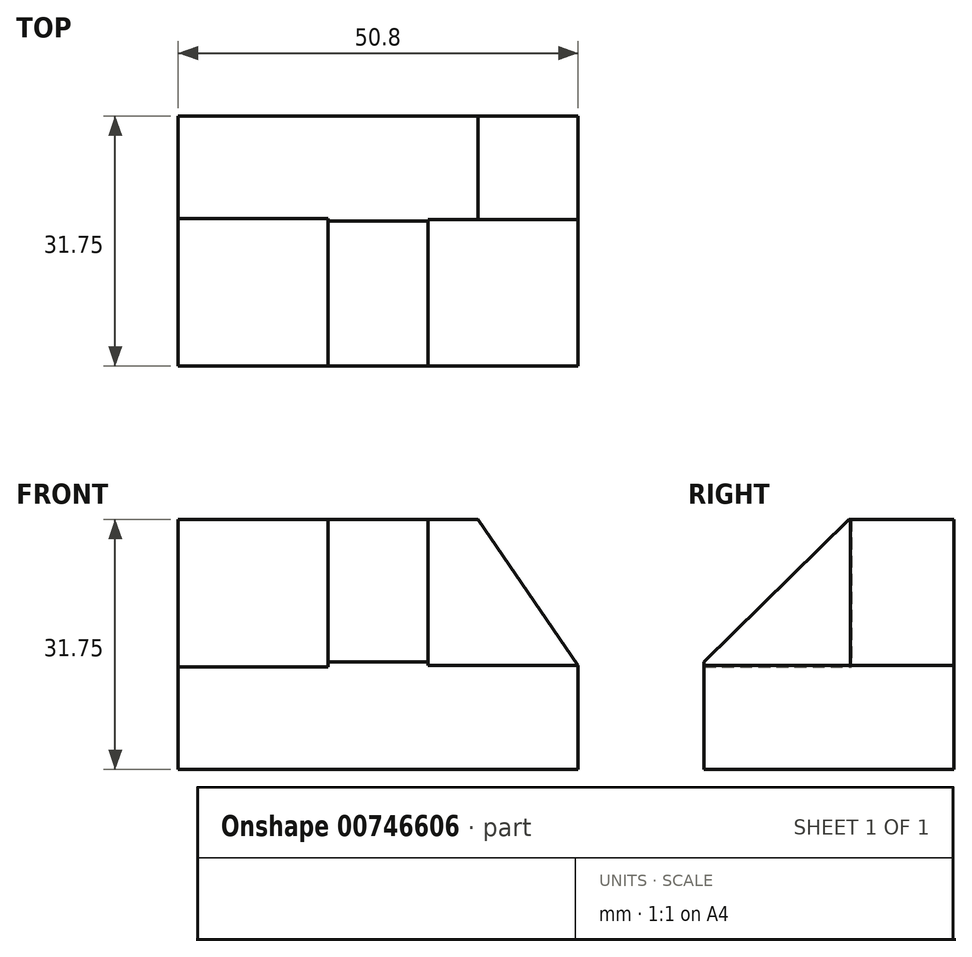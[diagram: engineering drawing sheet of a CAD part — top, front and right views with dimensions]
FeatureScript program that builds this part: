
annotation { "Feature Type Name" : "Feature", "Feature Type Description" : "" }
export const myFeature = defineFeature(function(context is Context, id is Id, definition is map)
    precondition{}
    {
        {
            var Q0;
            Q0=qCreatedBy(makeId("Front.planeOp"),FACE);
            var sketch = newSketch(context, id + "F0", { "sketchPlane" : qUnion([Q0])});
            skLineSegment(sketch, "E0.bottom", {"start": v(0, 0) * mm, "end": v(50.8, 0) * mm});
            skLineSegment(sketch, "E0.top", {"start": v(0, 31.75) * mm, "end": v(50.8, 31.75) * mm});
            skLineSegment(sketch, "E0.left", {"start": v(0, 0) * mm, "end": v(0, 31.75) * mm});
            skLineSegment(sketch, "E0.right", {"start": v(50.8, 0) * mm, "end": v(50.8, 31.75) * mm});
            skSolve(sketch);
        }
        {
            var Q0;
            Q0 = qSketchRegion(id + "F0", true);
            extrude(context, id + "F1", {"entities" : qUnion([Q0]), "depth" : 31.75 * mm, "offsetDistance" : 25.4 * mm});
        }
        {
            var Q0;
            Q0=qCreatedBy(makeId("Right.planeOp"),FACE);
            var sketch = newSketch(context, id + "F2", { "sketchPlane" : qUnion([Q0])});
            skLineSegment(sketch, "E1.bottom", {"start": v(-32.07, 32.06) * mm, "end": v(-13.02, 32.06) * mm});
            skLineSegment(sketch, "E1.top", {"start": v(-32.07, 13) * mm, "end": v(-13.02, 13) * mm});
            skLineSegment(sketch, "E1.left", {"start": v(-32.07, 32.06) * mm, "end": v(-32.07, 13) * mm});
            skLineSegment(sketch, "E1.right", {"start": v(-13.02, 32.06) * mm, "end": v(-13.02, 13) * mm});
            skSolve(sketch);
        }
        {
            var Q0;
            Q0 = qSketchRegion(id + "F2", true);
            extrude(context, id + "F3", {"entities" : qUnion([Q0]), "operationType" : NewBodyOperationType.REMOVE, "depth" : 19.05 * mm, "offsetDistance" : 25.4 * mm});
        }
        {
            var Q0;
            Q0=makeQuery(id+"F1.opExtrude","SWEPT_FACE",FACE,{"disambiguationData":[OSD([sQuery(id+"F0.wireOp",EDGE,"E0.right")])]});
            var sketch = newSketch(context, id + "F4", { "sketchPlane" : qUnion([Q0])});
            skLineSegment(sketch, "E2.bottom", {"start": v(-32.22, 32.25) * mm, "end": v(-13.17, 32.25) * mm});
            skLineSegment(sketch, "E2.top", {"start": v(-32.22, 13.2) * mm, "end": v(-13.17, 13.2) * mm});
            skLineSegment(sketch, "E2.left", {"start": v(-32.22, 32.25) * mm, "end": v(-32.22, 13.2) * mm});
            skLineSegment(sketch, "E2.right", {"start": v(-13.17, 32.25) * mm, "end": v(-13.17, 13.2) * mm});
            skSolve(sketch);
        }
        {
            var Q0;
            Q0 = qSketchRegion(id + "F4", true);
            extrude(context, id + "F5", {"entities" : qUnion([Q0]), "operationType" : NewBodyOperationType.REMOVE, "oppositeDirection" : true, "depth" : 19.05 * mm, "offsetDistance" : 25.4 * mm});
        }
        {
            var Q0;
            Q0=makeQuery(id+"F5.boolean.opBoolean","COPY",FACE,{"derivedFrom":makeQuery(id+"F5.opExtrude","CAP_FACE",FACE,{"disambiguationData":[OSD([sQuery(id+"F4.wireOp",EDGE,"E2.bottom"),sQuery(id+"F4.wireOp",EDGE,"E2.top"),sQuery(id+"F4.wireOp",EDGE,"E2.left"),sQuery(id+"F4.wireOp",EDGE,"E2.right")])],"isStart":false})});
            var sketch = newSketch(context, id + "F6", { "sketchPlane" : qUnion([Q0])});
            skLineSegment(sketch, "E3", {"start": v(-32.37, 13.04) * mm, "end": v(-13.02, 32.09) * mm});
            skLineSegment(sketch, "E4", {"start": v(-32.07, 32.09) * mm, "end": v(-32.37, 13.04) * mm});
            skLineSegment(sketch, "E5", {"start": v(-32.07, 32.09) * mm, "end": v(-13.02, 32.09) * mm});
            skSolve(sketch);
        }
        {
            var Q0;
            Q0 = qSketchRegion(id + "F6", true);
            extrude(context, id + "F7", {"entities" : qUnion([Q0]), "operationType" : NewBodyOperationType.REMOVE, "oppositeDirection" : true, "depth" : 12.7 * mm, "offsetDistance" : 25.4 * mm});
        }
        {
            var Q0;
            Q0=makeQuery(id+"F5.boolean.opBoolean","COPY",FACE,{"derivedFrom":makeQuery(id+"F5.opExtrude","SWEPT_FACE",FACE,{"disambiguationData":[OSD([sQuery(id+"F4.wireOp",EDGE,"E2.right")])]})});
            var sketch = newSketch(context, id + "F8", { "sketchPlane" : qUnion([Q0])});
            skLineSegment(sketch, "E6", {"start": v(38.1, 31.75) * mm, "end": v(50.8, 13.2) * mm});
            skLineSegment(sketch, "E7", {"start": v(50.8, 13.2) * mm, "end": v(31.75, 13.2) * mm});
            skLineSegment(sketch, "E8", {"start": v(31.75, 13.2) * mm, "end": v(31.75, 31.75) * mm});
            skLineSegment(sketch, "E9", {"start": v(31.75, 31.75) * mm, "end": v(38.1, 31.75) * mm});
            skSolve(sketch);
        }
        {
            var Q0;
            {var subQ0=sQuery(id+"F8.wireOp",EDGE,"E6");Q0=makeQuery(id+"F8.imprint","IMPRINT",FACE,{"disambiguationData":[TD([[makeQuery(id+"F8.imprint","IMPRINT",EDGE,{"derivedFrom":subQ0}),1.0]])]});}
            extrude(context, id + "F9", {"entities" : qUnion([Q0]), "operationType" : NewBodyOperationType.REMOVE, "oppositeDirection" : true, "depth" : 25.4 * mm, "offsetDistance" : 25.4 * mm});
        }
    });
